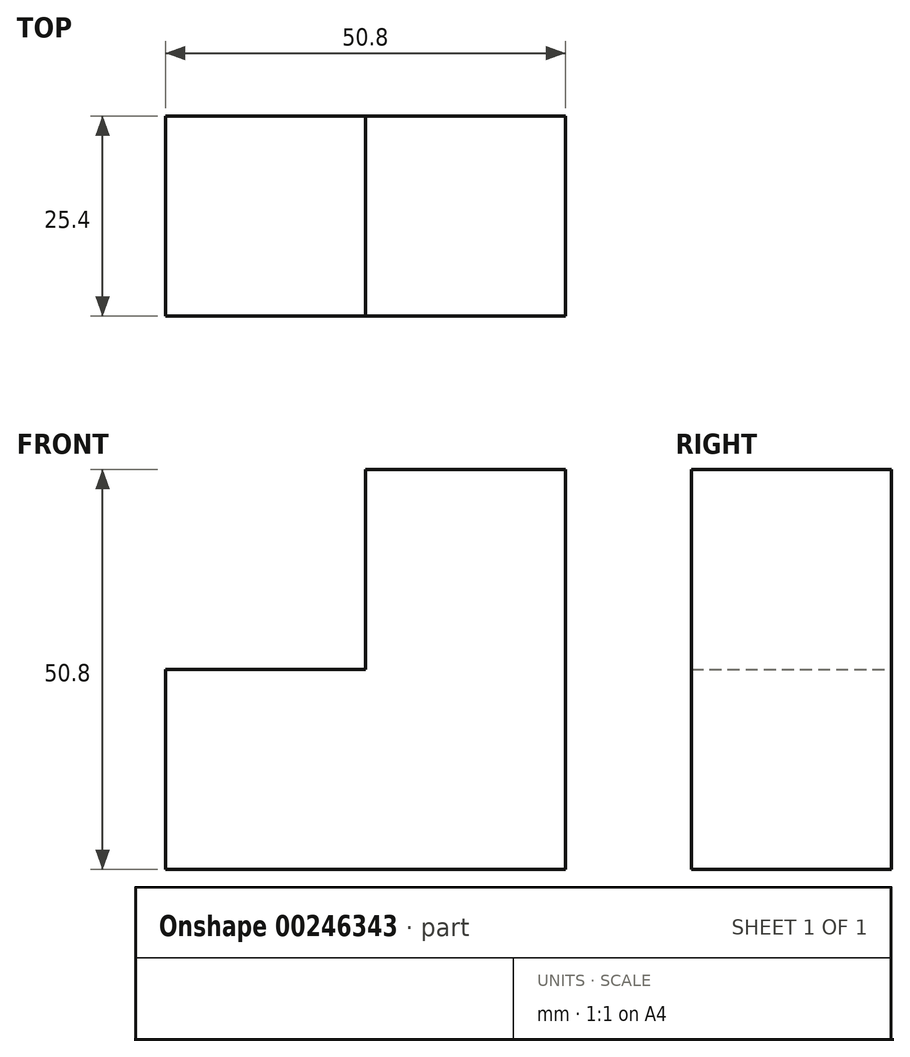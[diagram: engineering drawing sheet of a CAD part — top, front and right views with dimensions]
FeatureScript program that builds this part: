
annotation { "Feature Type Name" : "Feature", "Feature Type Description" : "" }
export const myFeature = defineFeature(function(context is Context, id is Id, definition is map)
    precondition{}
    {
        {
            var Q0;
            Q0=qCreatedBy(makeId("Front.planeOp"),FACE);
            var sketch = newSketch(context, id + "F0", { "sketchPlane" : qUnion([Q0])});
            skLineSegment(sketch, "E0", {"start": v(0, 0) * mm, "end": v(0, 50.8) * mm});
            skLineSegment(sketch, "E1", {"start": v(0, 0) * mm, "end": v(-50.8, 0) * mm});
            skLineSegment(sketch, "E2", {"start": v(-50.8, 0) * mm, "end": v(-50.8, 25.4) * mm});
            skLineSegment(sketch, "E3", {"start": v(-50.8, 25.4) * mm, "end": v(-25.4, 25.4) * mm});
            skLineSegment(sketch, "E4", {"start": v(-25.4, 25.4) * mm, "end": v(-25.4, 50.8) * mm});
            skLineSegment(sketch, "E5", {"start": v(-25.4, 50.8) * mm, "end": v(0, 50.8) * mm});
            skSolve(sketch);
        }
        {
            var Q0;
            Q0 = qSketchRegion(id + "F0", true);
            extrude(context, id + "F1", {"entities" : qUnion([Q0]), "depth" : 25.4 * mm});
        }
    });
